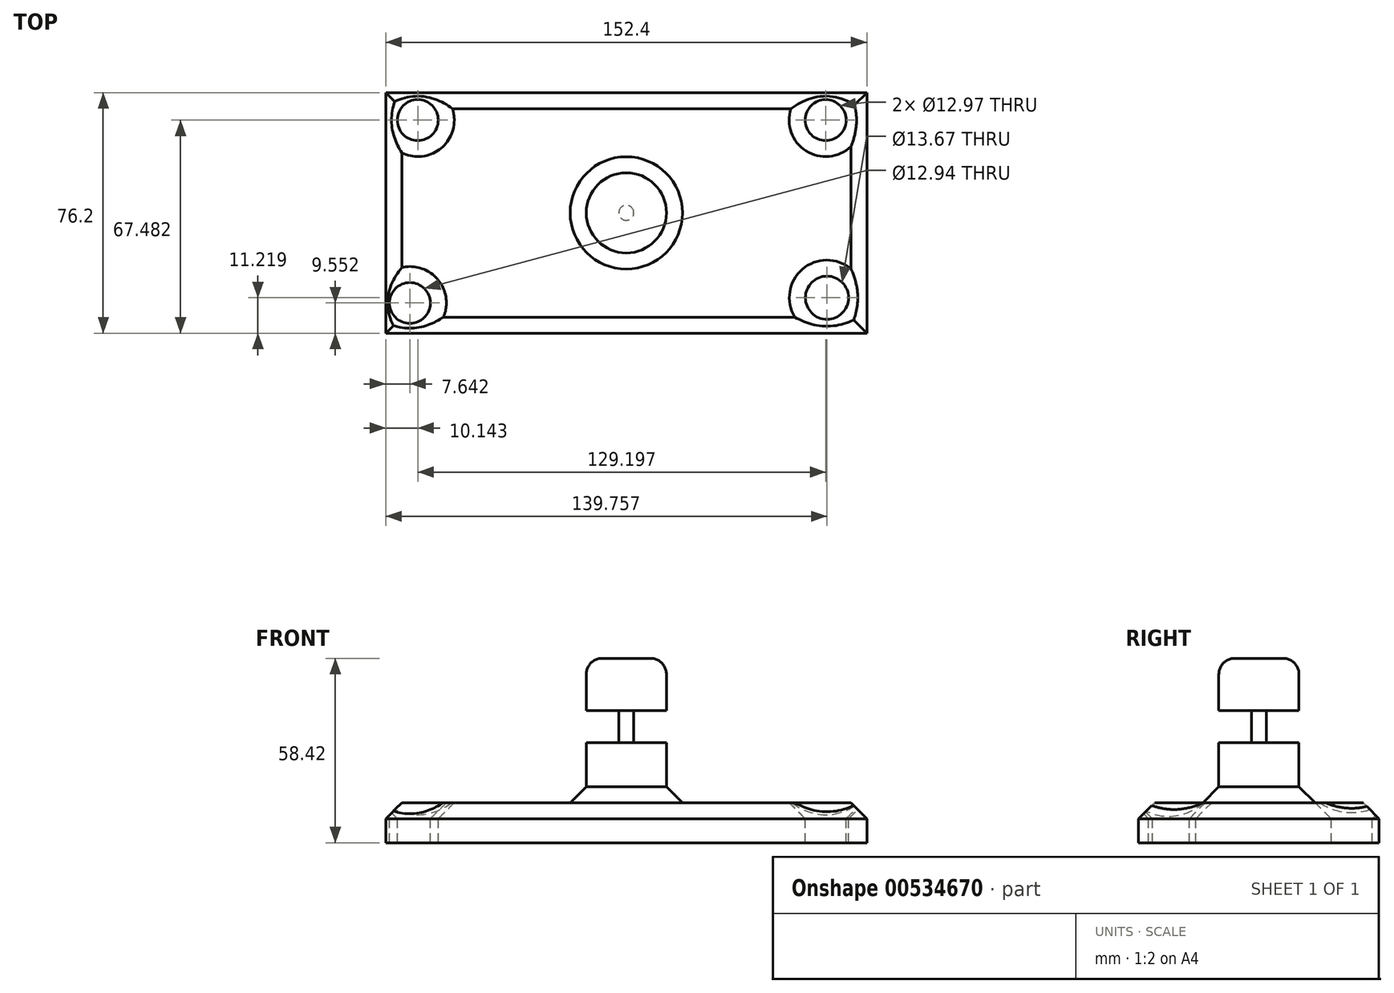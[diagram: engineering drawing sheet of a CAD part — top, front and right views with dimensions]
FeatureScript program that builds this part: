
annotation { "Feature Type Name" : "Feature", "Feature Type Description" : "" }
export const myFeature = defineFeature(function(context is Context, id is Id, definition is map)
    precondition{}
    {
        {
            var Q0;
            Q0=qCreatedBy(makeId("Top.planeOp"),FACE);
            var sketch = newSketch(context, id + "F0", { "sketchPlane" : qUnion([Q0])});
            skLineSegment(sketch, "E0.bottom", {"start": v(76.2, 38.1) * mm, "end": v(-76.2, 38.1) * mm});
            skLineSegment(sketch, "E0.top", {"start": v(76.2, -38.1) * mm, "end": v(-76.2, -38.1) * mm});
            skLineSegment(sketch, "E0.left", {"start": v(76.2, 38.1) * mm, "end": v(76.2, -38.1) * mm});
            skLineSegment(sketch, "E0.right", {"start": v(-76.2, 38.1) * mm, "end": v(-76.2, -38.1) * mm});
            skPoint(sketch, "E0.middle", {"position": v(0, 0) * mm});
            skLineSegment(sketch, "E1.bottom", {"start": v(76.2, 54.78) * mm, "end": v(76.2, 54.78) * mm});
            skLineSegment(sketch, "E1.top", {"start": v(76.2, 21.42) * mm, "end": v(76.2, 21.42) * mm});
            skLineSegment(sketch, "E1.left", {"start": v(76.2, 54.78) * mm, "end": v(76.2, 21.42) * mm});
            skPoint(sketch, "E1.middle", {"position": v(76.2, 38.1) * mm});
            skSolve(sketch);
        }
        {
            var Q0;
            {var subQ1=sQuery(id+"F0.wireOp",EDGE,"E0.bottom");Q0=makeQuery(id+"F0.imprint","IMPRINT",FACE,{"disambiguationData":[TD([[makeQuery(id+"F0.imprint","IMPRINT",EDGE,{"derivedFrom":subQ1}),1.0]])]});}
            extrude(context, id + "F1", {"entities" : qUnion([Q0]), "depth" : 12.7 * mm, "offsetDistance" : 25.4 * mm});
        }
        {
            var Q0;
            Q0=makeQuery(id+"F1.opExtrude","CAP_FACE",FACE,{"disambiguationData":[OSD([sQuery(id+"F0.wireOp",EDGE,"E0.bottom"),sQuery(id+"F0.wireOp",EDGE,"E0.top"),sQuery(id+"F0.wireOp",EDGE,"E0.left"),sQuery(id+"F0.wireOp",EDGE,"E0.right"),sQuery(id+"F0.wireOp",EDGE,"E1.left")])],"isStart":false});
            var sketch = newSketch(context, id + "F2", { "sketchPlane" : qUnion([Q0])});
            skCircle(sketch, "E2", {"center": v(-66.06, 29.38) * mm, "radius": 6.48 * mm});
            skCircle(sketch, "E3", {"center": v(-68.56, -28.55) * mm, "radius": 6.47 * mm});
            skCircle(sketch, "E4", {"center": v(63.14, 29.38) * mm, "radius": 6.48 * mm});
            skCircle(sketch, "E5", {"center": v(63.56, -26.88) * mm, "radius": 6.84 * mm});
            skSolve(sketch);
        }
        {
            var Q0;
            Q0=makeQuery(id+"Ff8QWj8EbTMcigt_1.opExtrude","CAP_FACE",FACE,{"disambiguationData":[OSD([sQuery(id+"F0.wireOp",EDGE,"E0.bottom"),sQuery(id+"F0.wireOp",EDGE,"E0.top"),sQuery(id+"F0.wireOp",EDGE,"E0.left"),sQuery(id+"F0.wireOp",EDGE,"E0.right"),sQuery(id+"F0.wireOp",EDGE,"E1.left")])],"isStart":false});
            var sketch = newSketch(context, id + "F3", { "sketchPlane" : qUnion([Q0])});
            skCircle(sketch, "E6", {"center": v(-66.49, 28.62) * mm, "radius": 7.83 * mm});
            skCircle(sketch, "E7", {"center": v(-67.14, -24.88) * mm, "radius": 7.52 * mm});
            skCircle(sketch, "E8", {"center": v(60.85, 29.54) * mm, "radius": 7.64 * mm});
            skCircle(sketch, "E9", {"center": v(62.72, -24.26) * mm, "radius": 9.4 * mm});
            skSolve(sketch);
        }
        {
            var Q0;
            Q0=makeQuery(id+"F3.imprint","IMPRINT",FACE,{"disambiguationData":[TD([[makeQuery(id+"F3.imprint","IMPRINT",EDGE,{"derivedFrom":sQuery(id+"F3.wireOp",EDGE,"E6")}),1.0]])]});
            var Q1;
            Q1=makeQuery(id+"F3.imprint","IMPRINT",FACE,{"disambiguationData":[TD([[makeQuery(id+"F3.imprint","IMPRINT",EDGE,{"derivedFrom":sQuery(id+"F3.wireOp",EDGE,"E8")}),1.0]])]});
            var Q2;
            Q2=makeQuery(id+"F3.imprint","IMPRINT",FACE,{"disambiguationData":[TD([[makeQuery(id+"F3.imprint","IMPRINT",EDGE,{"derivedFrom":sQuery(id+"F3.wireOp",EDGE,"E9")}),1.0]])]});
            var Q3;
            Q3=makeQuery(id+"F3.imprint","IMPRINT",FACE,{"disambiguationData":[TD([[makeQuery(id+"F3.imprint","IMPRINT",EDGE,{"derivedFrom":sQuery(id+"F3.wireOp",EDGE,"E7")}),1.0]])]});
            var Q4;
            Q4=makeQuery(id+"F2.imprint","IMPRINT",FACE,{"disambiguationData":[TD([[makeQuery(id+"F2.imprint","IMPRINT",EDGE,{"derivedFrom":sQuery(id+"F2.wireOp",EDGE,"E5")}),1.0]])]});
            var Q5;
            Q5=makeQuery(id+"F2.imprint","IMPRINT",FACE,{"disambiguationData":[TD([[makeQuery(id+"F2.imprint","IMPRINT",EDGE,{"derivedFrom":sQuery(id+"F2.wireOp",EDGE,"E4")}),1.0]])]});
            var Q6;
            Q6=makeQuery(id+"F2.imprint","IMPRINT",FACE,{"disambiguationData":[TD([[makeQuery(id+"F2.imprint","IMPRINT",EDGE,{"derivedFrom":sQuery(id+"F2.wireOp",EDGE,"E3")}),1.0]])]});
            var Q7;
            Q7=makeQuery(id+"F2.imprint","IMPRINT",FACE,{"disambiguationData":[TD([[makeQuery(id+"F2.imprint","IMPRINT",EDGE,{"derivedFrom":sQuery(id+"F2.wireOp",EDGE,"E2")}),1.0]])]});
            extrude(context, id + "F4", {"entities" : qUnion([Q0, Q1, Q2, Q3, Q4, Q5, Q6, Q7]), "operationType" : NewBodyOperationType.REMOVE, "oppositeDirection" : true, "depth" : 25.4 * mm, "offsetDistance" : 25.4 * mm});
        }
        {
            var Q0;
            Q0=qCreatedBy(makeId("Front.planeOp"),FACE);
            var sketch = newSketch(context, id + "F5", { "sketchPlane" : qUnion([Q0])});
            skLineSegment(sketch, "E10.bottom", {"start": v(0, 58.42) * mm, "end": v(12.7, 58.42) * mm});
            skLineSegment(sketch, "E10.top", {"start": v(0, 12.7) * mm, "end": v(12.7, 12.7) * mm});
            skLineSegment(sketch, "E10.left", {"start": v(0, 58.42) * mm, "end": v(0, 12.7) * mm});
            skLineSegment(sketch, "E10.right", {"start": v(12.7, 58.42) * mm, "end": v(12.7, 12.7) * mm});
            skSolve(sketch);
        }
        {
            var Q0;
            Q0=makeQuery(id+"F5.imprint","IMPRINT",FACE,{"disambiguationData":[TD([[makeQuery(id+"F5.imprint","IMPRINT",EDGE,{"derivedFrom":sQuery(id+"F5.wireOp",EDGE,"E10.bottom")}),-1.0]])]});
            var Q1;
            Q1=sQuery(id+"F5.wireOp",EDGE,"E10.left");
            revolve(context, id + "F6", {"operationType" : NewBodyOperationType.ADD, "entities" : qUnion([Q0]), "axis" : qUnion([Q1]), "revolveType" : RevolveType.FULL});
        }
        {
            var Q0;
            Q0=qCreatedBy(makeId("Front.planeOp"),FACE);
            var sketch = newSketch(context, id + "F7", { "sketchPlane" : qUnion([Q0])});
            skLineSegment(sketch, "E11.bottom", {"start": v(2.38, 41.89) * mm, "end": v(15.08, 41.89) * mm});
            skLineSegment(sketch, "E11.top", {"start": v(2.38, 31.73) * mm, "end": v(15.08, 31.73) * mm});
            skLineSegment(sketch, "E11.left", {"start": v(2.38, 41.89) * mm, "end": v(2.38, 31.73) * mm});
            skLineSegment(sketch, "E11.right", {"start": v(15.08, 41.89) * mm, "end": v(15.08, 31.73) * mm});
            skSolve(sketch);
        }
        {
            var Q0;
            Q0=makeQuery(id+"F7.imprint","IMPRINT",FACE,{"disambiguationData":[TD([[makeQuery(id+"F7.imprint","IMPRINT",EDGE,{"derivedFrom":sQuery(id+"F7.wireOp",EDGE,"E11.bottom")}),-1.0]])]});
            var Q1;
            Q1=makeQuery(id+"F6.opRevolve","SWEPT_FACE",FACE,{"disambiguationData":[OSD([sQuery(id+"F5.wireOp",EDGE,"E10.right")])]});
            revolve(context, id + "F8", {"operationType" : NewBodyOperationType.REMOVE, "entities" : qUnion([Q0]), "axis" : qUnion([Q1]), "revolveType" : RevolveType.FULL, "oppositeDirection" : true});
        }
        {
            var Q0;
            Q0=makeQuery(id+"F6.opRevolve","SWEPT_EDGE",EDGE,{"disambiguationData":[OSD([sQuery(id+"F5.wireOp",EDGE,"E10.bottom"),sQuery(id+"F5.wireOp",EDGE,"E10.right")])]});
            var Q1;
            Q1=makeQuery(id+"F6.opRevolve","SWEPT_EDGE",EDGE,{"disambiguationData":[OSD([sQuery(id+"F5.wireOp",EDGE,"E10.top"),sQuery(id+"F5.wireOp",EDGE,"E10.right")])]});
            fillet(context, id + "F9", {"entities" : qUnion([Q0, Q1]), "radius" : 5.08 * mm, "tangentPropagation" : true, "allowEdgeOverflow" : false});
        }
        {
            var Q0;
            Q0=makeQuery(id+"F1.opExtrude","CAP_FACE",FACE,{"disambiguationData":[OSD([sQuery(id+"F0.wireOp",EDGE,"E0.bottom"),sQuery(id+"F0.wireOp",EDGE,"E0.top"),sQuery(id+"F0.wireOp",EDGE,"E0.left"),sQuery(id+"F0.wireOp",EDGE,"E0.right"),sQuery(id+"F0.wireOp",EDGE,"E1.left")])],"isStart":false});
            chamfer(context, id + "F10", {"entities" : qUnion([Q0]), "width" : 5.08 * mm, "tangentPropagation" : true});
        }
    });
